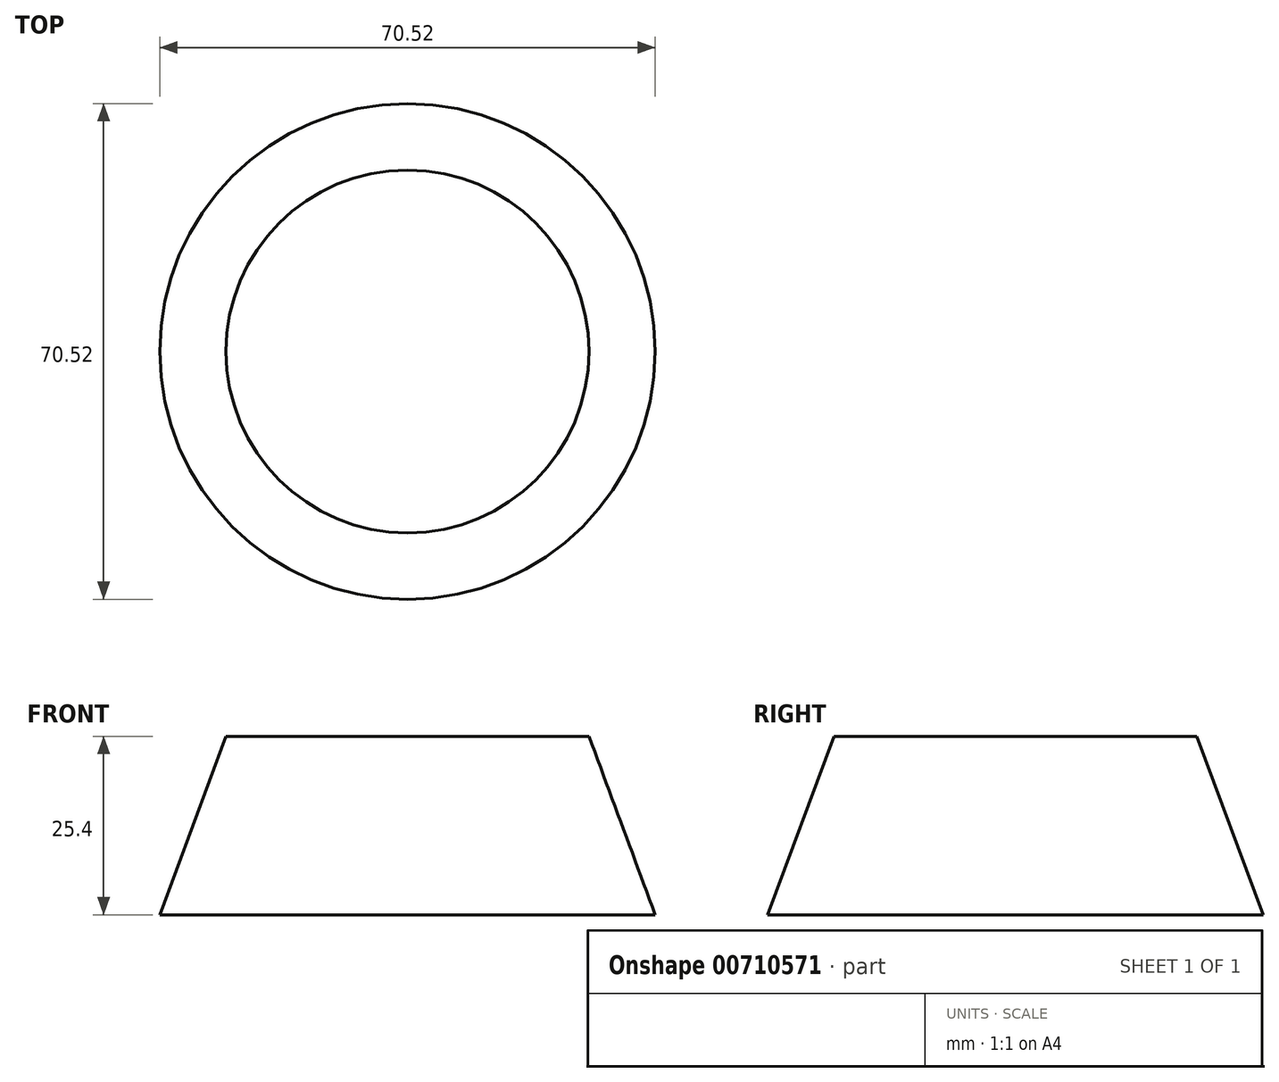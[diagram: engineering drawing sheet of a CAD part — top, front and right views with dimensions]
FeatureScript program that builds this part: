
annotation { "Feature Type Name" : "Feature", "Feature Type Description" : "" }
export const myFeature = defineFeature(function(context is Context, id is Id, definition is map)
    precondition{}
    {
        {
            var Q0;
            Q0=qCreatedBy(makeId("Top.planeOp"),FACE);
            var sketch = newSketch(context, id + "F0", { "sketchPlane" : qUnion([Q0])});
            skCircle(sketch, "E0", {"center": v(0, 0) * mm, "radius": 35.26 * mm});
            skSolve(sketch);
        }
        {
            var Q0;
            Q0=makeQuery(id+"F0.imprint","IMPRINT",FACE,{"disambiguationData":[TD([[makeQuery(id+"F0.imprint","IMPRINT",EDGE,{"derivedFrom":sQuery(id+"F0.wireOp",EDGE,"E0")}),1.0]])]});
            cPlane(context, id + "F1", {"entities" : qUnion([Q0]), "cplaneType" : CPlaneType.OFFSET, "offset" : 25.4 * mm, "width" : 152.4 * mm, "height" : 152.4 * mm});
        }
        {
            var Q0;
            Q0=qCreatedBy(id+"F1.planeOp",FACE);
            var sketch = newSketch(context, id + "F2", { "sketchPlane" : qUnion([Q0])});
            skCircle(sketch, "E1", {"center": v(0, 0) * mm, "radius": 25.83 * mm});
            skSolve(sketch);
        }
        {
            var Q0;
            Q0=makeQuery(id+"F0.imprint","IMPRINT",FACE,{"disambiguationData":[TD([[makeQuery(id+"F0.imprint","IMPRINT",EDGE,{"derivedFrom":sQuery(id+"F0.wireOp",EDGE,"E0")}),1.0]])]});
            var Q1;
            Q1=makeQuery(id+"F2.imprint","IMPRINT",FACE,{"disambiguationData":[TD([[makeQuery(id+"F2.imprint","IMPRINT",EDGE,{"derivedFrom":sQuery(id+"F2.wireOp",EDGE,"E1")}),1.0]])]});
            loft(context, id + "F3", {"sheetProfilesArray" : [{ "sheetProfileEntities" : qUnion([Q0]) }, { "sheetProfileEntities" : qUnion([Q1]) }]});
        }
    });
